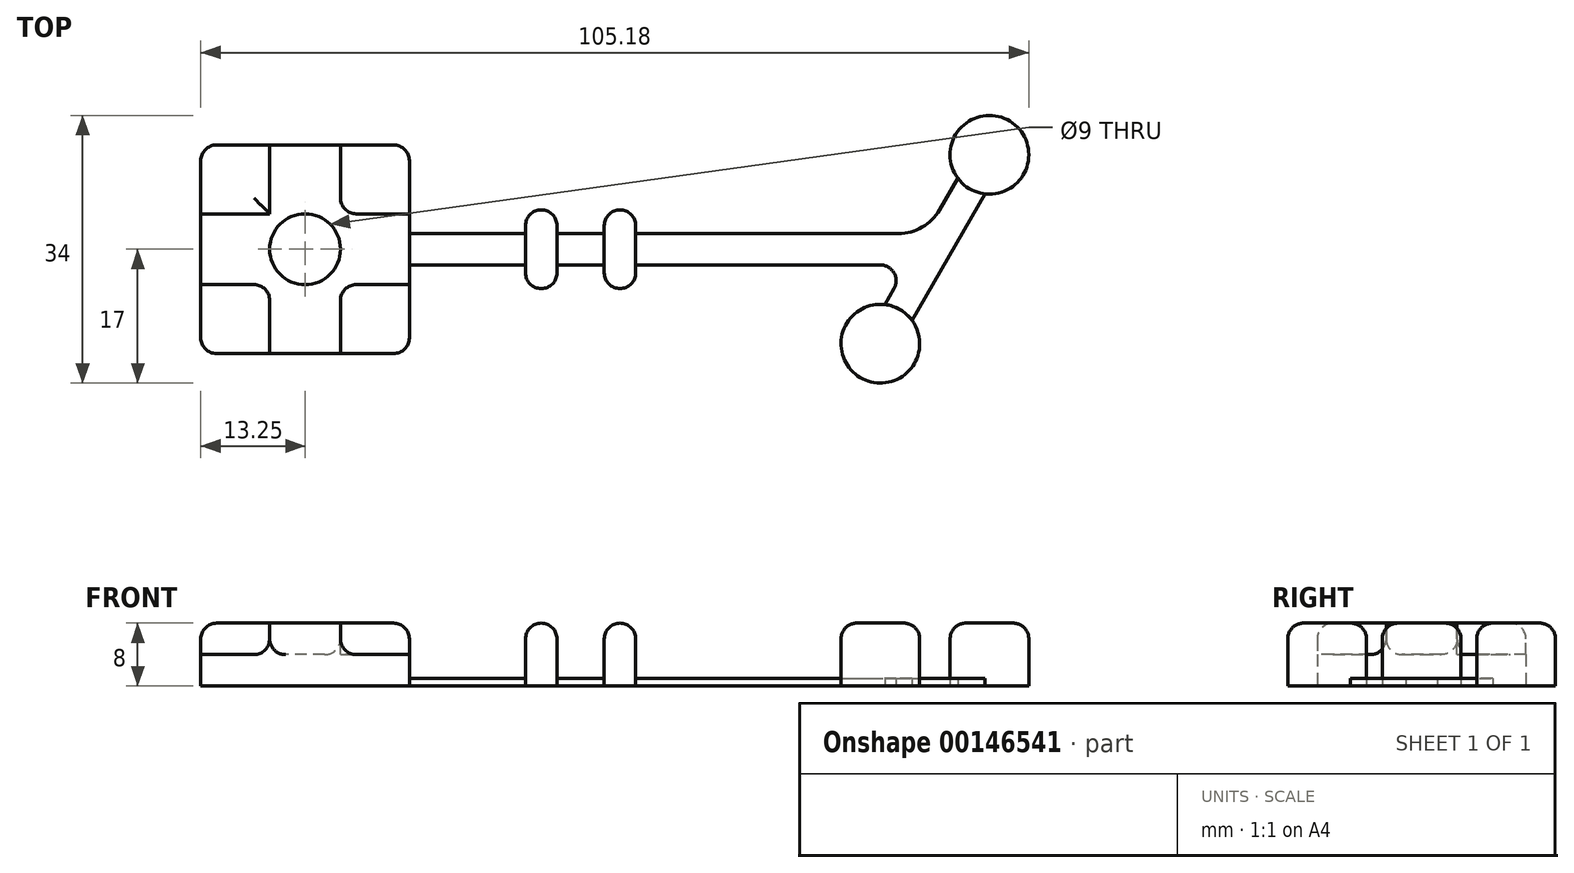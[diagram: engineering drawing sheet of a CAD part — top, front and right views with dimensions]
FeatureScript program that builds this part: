
annotation { "Feature Type Name" : "Feature", "Feature Type Description" : "" }
export const myFeature = defineFeature(function(context is Context, id is Id, definition is map)
    precondition{}
    {
        {
            var Q0;
            Q0=qCreatedBy(makeId("Top.planeOp"),FACE);
            var sketch = newSketch(context, id + "F0", { "sketchPlane" : qUnion([Q0])});
            skLineSegment(sketch, "E0.bottom", {"start": v(13.25, -13.25) * mm, "end": v(-13.25, -13.25) * mm});
            skLineSegment(sketch, "E0.top", {"start": v(13.25, 13.25) * mm, "end": v(-13.25, 13.25) * mm});
            skLineSegment(sketch, "E0.left", {"start": v(13.25, -13.25) * mm, "end": v(13.25, 13.25) * mm});
            skLineSegment(sketch, "E0.right", {"start": v(-13.25, -13.25) * mm, "end": v(-13.25, 13.25) * mm});
            skPoint(sketch, "E0.middle", {"position": v(0, 0) * mm});
            skLineSegment(sketch, "E1", {"start": v(0, 0) * mm, "end": v(80, 0) * mm, "construction": true});
            skLineSegment(sketch, "E2", {"start": v(80, 0) * mm, "end": v(86.93, 12) * mm, "construction": true});
            skCircle(sketch, "E3", {"center": v(86.93, 12) * mm, "radius": 5 * mm});
            skCircle(sketch, "E4", {"center": v(73.07, -12) * mm, "radius": 5 * mm});
            skLineSegment(sketch, "E5.bottom", {"start": v(32, -3) * mm, "end": v(28, -3) * mm});
            skLineSegment(sketch, "E5.top", {"start": v(32, 3) * mm, "end": v(28, 3) * mm});
            skLineSegment(sketch, "E5.left", {"start": v(32, -3) * mm, "end": v(32, 3) * mm});
            skLineSegment(sketch, "E5.right", {"start": v(28, -3) * mm, "end": v(28, 3) * mm});
            skPoint(sketch, "E5.middle", {"position": v(30, 0) * mm});
            skLineSegment(sketch, "E6.bottom", {"start": v(42, -3) * mm, "end": v(38, -3) * mm});
            skLineSegment(sketch, "E6.top", {"start": v(42, 3) * mm, "end": v(38, 3) * mm});
            skLineSegment(sketch, "E6.left", {"start": v(42, -3) * mm, "end": v(42, 3) * mm});
            skLineSegment(sketch, "E6.right", {"start": v(38, -3) * mm, "end": v(38, 3) * mm});
            skPoint(sketch, "E6.middle", {"position": v(40, 0) * mm});
            skLineSegment(sketch, "E7", {"start": v(13.25, 2) * mm, "end": v(28, 2) * mm});
            skLineSegment(sketch, "E8", {"start": v(32, 2) * mm, "end": v(38, 2) * mm});
            skLineSegment(sketch, "E9", {"start": v(42, 2) * mm, "end": v(78.85, 2) * mm});
            skLineSegment(sketch, "E10.MirrorCS", {"start": v(42, -2) * mm, "end": v(76.54, -2) * mm});
            skLineSegment(sketch, "E11.MirrorCS", {"start": v(32, -2) * mm, "end": v(38, -2) * mm});
            skLineSegment(sketch, "E12.MirrorCS", {"start": v(13.25, -2) * mm, "end": v(28, -2) * mm});
            skLineSegment(sketch, "E13.0", {"start": v(73.63, -7.03) * mm, "end": v(76.54, -2) * mm});
            skLineSegment(sketch, "E14.MirrorCS", {"start": v(77.1, -9.03) * mm, "end": v(86.37, 7.03) * mm});
            skLineSegment(sketch, "E15.trimOffspring", {"start": v(78.85, 2) * mm, "end": v(82.9, 9.03) * mm});
            skArc(sketch, "E16", {"start": v(32, 3) * mm, "mid": v(30, 5) * mm, "end": v(28, 3) * mm});
            skArc(sketch, "E17", {"start": v(38, 3) * mm, "mid": v(40, 5) * mm, "end": v(42, 3) * mm});
            skArc(sketch, "E18.MirrorCS", {"start": v(38, -3) * mm, "mid": v(40, -5) * mm, "end": v(42, -3) * mm});
            skArc(sketch, "E19.MirrorCS", {"start": v(32, -3) * mm, "mid": v(30, -5) * mm, "end": v(28, -3) * mm});
            skSolve(sketch);
        }
        {
            var Q0;
            {var subQ3=sQuery(id+"F0.wireOp",EDGE,"E0.bottom");Q0=makeQuery(id+"F0.imprint","IMPRINT",FACE,{"disambiguationData":[TD([[makeQuery(id+"F0.imprint","IMPRINT",EDGE,{"derivedFrom":subQ3}),-1.0]])]});}
            var Q1;
            Q1=makeQuery(id+"F0.imprint","IMPRINT",FACE,{"disambiguationData":[TD([[makeQuery(id+"F0.imprint","IMPRINT",EDGE,{"derivedFrom":sQuery(id+"F0.wireOp",EDGE,"E5.top")}),-1.0]])]});
            var Q2;
            {var subQ8=sQuery(id+"F0.wireOp",EDGE,"E5.bottom");Q2=makeQuery(id+"F0.imprint","IMPRINT",FACE,{"disambiguationData":[TD([[makeQuery(id+"F0.imprint","IMPRINT",EDGE,{"derivedFrom":subQ8}),-1.0]])]});}
            var Q3;
            Q3=makeQuery(id+"F0.imprint","IMPRINT",FACE,{"disambiguationData":[TD([[makeQuery(id+"F0.imprint","IMPRINT",EDGE,{"derivedFrom":sQuery(id+"F0.wireOp",EDGE,"E5.bottom")}),1.0]])]});
            var Q4;
            Q4=makeQuery(id+"F0.imprint","IMPRINT",FACE,{"disambiguationData":[TD([[makeQuery(id+"F0.imprint","IMPRINT",EDGE,{"derivedFrom":sQuery(id+"F0.wireOp",EDGE,"E6.top")}),-1.0]])]});
            var Q5;
            {var subQ4=sQuery(id+"F0.wireOp",EDGE,"E6.bottom");Q5=makeQuery(id+"F0.imprint","IMPRINT",FACE,{"disambiguationData":[TD([[makeQuery(id+"F0.imprint","IMPRINT",EDGE,{"derivedFrom":subQ4}),-1.0]])]});}
            var Q6;
            Q6=makeQuery(id+"F0.imprint","IMPRINT",FACE,{"disambiguationData":[TD([[makeQuery(id+"F0.imprint","IMPRINT",EDGE,{"derivedFrom":sQuery(id+"F0.wireOp",EDGE,"E6.bottom")}),1.0]])]});
            var Q7;
            {var subQ0=sQuery(id+"F0.wireOp",EDGE,"E3");var subQ1=makeQuery(id+"F0.imprint","INTERSECT",VERTEX,{"derivedFrom":[subQ0,sQuery(id+"F0.wireOp",EDGE,"E14.MirrorCS")]});Q7=makeQuery(id+"F0.imprint","IMPRINT",FACE,{"disambiguationData":[TD([[makeQuery(id+"F0.imprint","IMPRINT",EDGE,{"disambiguationData":[TD([[subQ1,1.0]])],"derivedFrom":subQ0}),1.0]])]});}
            var Q8;
            {var subQ0=sQuery(id+"F0.wireOp",EDGE,"E4");var subQ1=makeQuery(id+"F0.imprint","INTERSECT",VERTEX,{"derivedFrom":[subQ0,sQuery(id+"F0.wireOp",EDGE,"E13.0")]});Q8=makeQuery(id+"F0.imprint","IMPRINT",FACE,{"disambiguationData":[TD([[makeQuery(id+"F0.imprint","IMPRINT",EDGE,{"disambiguationData":[TD([[subQ1,1.0]])],"derivedFrom":subQ0}),1.0]])]});}
            extrude(context, id + "F1", {"entities" : qUnion([Q0, Q1, Q2, Q3, Q4, Q5, Q6, Q7, Q8]), "depth" : 8 * mm});
        }
        {
            var Q0;
            {var subQ0=sQuery(id+"F0.wireOp",EDGE,"E7");Q0=makeQuery(id+"F0.imprint","IMPRINT",FACE,{"disambiguationData":[TD([[makeQuery(id+"F0.imprint","IMPRINT",EDGE,{"derivedFrom":subQ0}),-1.0]])]});}
            var Q1;
            {var subQ0=sQuery(id+"F0.wireOp",EDGE,"E8");Q1=makeQuery(id+"F0.imprint","IMPRINT",FACE,{"disambiguationData":[TD([[makeQuery(id+"F0.imprint","IMPRINT",EDGE,{"derivedFrom":subQ0}),-1.0]])]});}
            var Q2;
            {var subQ0=sQuery(id+"F0.wireOp",EDGE,"E9");Q2=makeQuery(id+"F0.imprint","IMPRINT",FACE,{"disambiguationData":[TD([[makeQuery(id+"F0.imprint","IMPRINT",EDGE,{"derivedFrom":subQ0}),-1.0]])]});}
            extrude(context, id + "F2", {"entities" : qUnion([Q0, Q1, Q2]), "operationType" : NewBodyOperationType.ADD, "depth" : 1 * mm});
        }
        {
            var Q0;
            Q0=makeQuery(id+"F1.opExtrude","CAP_FACE",FACE,{"disambiguationData":[OSD([sQuery(id+"F0.wireOp",EDGE,"E5.left"),sQuery(id+"F0.wireOp",EDGE,"E5.right"),sQuery(id+"F0.wireOp",EDGE,"E16"),sQuery(id+"F0.wireOp",EDGE,"E19.MirrorCS")])],"isStart":false});
            var Q1;
            Q1=makeQuery(id+"F1.opExtrude","CAP_FACE",FACE,{"disambiguationData":[OSD([sQuery(id+"F0.wireOp",EDGE,"E6.left"),sQuery(id+"F0.wireOp",EDGE,"E6.right"),sQuery(id+"F0.wireOp",EDGE,"E17"),sQuery(id+"F0.wireOp",EDGE,"E18.MirrorCS")])],"isStart":false});
            var Q2;
            Q2=makeQuery(id+"F1.opExtrude","CAP_FACE",FACE,{"disambiguationData":[OSD([sQuery(id+"F0.wireOp",EDGE,"E3")])],"isStart":false});
            var Q3;
            Q3=makeQuery(id+"F1.opExtrude","CAP_FACE",FACE,{"disambiguationData":[OSD([sQuery(id+"F0.wireOp",EDGE,"E4")])],"isStart":false});
            fillet(context, id + "F3", {"entities" : qUnion([Q0, Q1, Q2, Q3]), "radius" : 2 * mm, "tangentPropagation" : true, "allowEdgeOverflow" : false});
        }
        {
            var Q0;
            Q0=makeQuery(id+"F2.opExtrude","SWEPT_EDGE",EDGE,{"disambiguationData":[OSD([sQuery(id+"F0.wireOp",EDGE,"E0.left"),sQuery(id+"F0.wireOp",EDGE,"E12.MirrorCS")])]});
            var Q1;
            Q1=makeQuery(id+"F2.opExtrude","SWEPT_EDGE",EDGE,{"disambiguationData":[OSD([sQuery(id+"F0.wireOp",EDGE,"E5.right"),sQuery(id+"F0.wireOp",EDGE,"E12.MirrorCS")])]});
            var Q2;
            Q2=makeQuery(id+"F2.opExtrude","SWEPT_EDGE",EDGE,{"disambiguationData":[OSD([sQuery(id+"F0.wireOp",EDGE,"E6.right"),sQuery(id+"F0.wireOp",EDGE,"E11.MirrorCS")])]});
            var Q3;
            Q3=makeQuery(id+"F2.opExtrude","SWEPT_EDGE",EDGE,{"disambiguationData":[OSD([sQuery(id+"F0.wireOp",EDGE,"E5.left"),sQuery(id+"F0.wireOp",EDGE,"E11.MirrorCS")])]});
            var Q4;
            Q4=makeQuery(id+"F2.opExtrude","SWEPT_EDGE",EDGE,{"disambiguationData":[OSD([sQuery(id+"F0.wireOp",EDGE,"E6.left"),sQuery(id+"F0.wireOp",EDGE,"E10.MirrorCS")])]});
            var Q5;
            Q5=makeQuery(id+"F2.opExtrude","SWEPT_EDGE",EDGE,{"disambiguationData":[OSD([sQuery(id+"F0.wireOp",EDGE,"E0.left"),sQuery(id+"F0.wireOp",EDGE,"E7")])]});
            var Q6;
            Q6=makeQuery(id+"F2.opExtrude","SWEPT_EDGE",EDGE,{"disambiguationData":[OSD([sQuery(id+"F0.wireOp",EDGE,"E5.left"),sQuery(id+"F0.wireOp",EDGE,"E8")])]});
            var Q7;
            Q7=makeQuery(id+"F2.opExtrude","SWEPT_EDGE",EDGE,{"disambiguationData":[OSD([sQuery(id+"F0.wireOp",EDGE,"E6.left"),sQuery(id+"F0.wireOp",EDGE,"E9")])]});
            var Q8;
            Q8=makeQuery(id+"F2.opExtrude","SWEPT_EDGE",EDGE,{"disambiguationData":[OSD([sQuery(id+"F0.wireOp",EDGE,"E4"),sQuery(id+"F0.wireOp",EDGE,"E14.MirrorCS")])]});
            var Q9;
            Q9=makeQuery(id+"F2.opExtrude","SWEPT_EDGE",EDGE,{"disambiguationData":[OSD([sQuery(id+"F0.wireOp",EDGE,"E3"),sQuery(id+"F0.wireOp",EDGE,"E14.MirrorCS")])]});
            var Q10;
            Q10=makeQuery(id+"F2.opExtrude","SWEPT_EDGE",EDGE,{"disambiguationData":[OSD([sQuery(id+"F0.wireOp",EDGE,"E10.MirrorCS"),sQuery(id+"F0.wireOp",EDGE,"E13.0")])]});
            var Q11;
            Q11=makeQuery(id+"F2.opExtrude","SWEPT_EDGE",EDGE,{"disambiguationData":[OSD([sQuery(id+"F0.wireOp",EDGE,"E5.right"),sQuery(id+"F0.wireOp",EDGE,"E7")])]});
            var Q12;
            Q12=makeQuery(id+"F2.opExtrude","SWEPT_EDGE",EDGE,{"disambiguationData":[OSD([sQuery(id+"F0.wireOp",EDGE,"E6.right"),sQuery(id+"F0.wireOp",EDGE,"E8")])]});
            fillet(context, id + "F4", {"entities" : qUnion([Q0, Q1, Q2, Q3, Q4, Q5, Q6, Q7, Q8, Q9, Q10, Q11, Q12]), "radius" : 2 * mm, "tangentPropagation" : true, "allowEdgeOverflow" : false});
        }
        {
            var Q0;
            Q0=makeQuery(id+"F2.opExtrude","SWEPT_EDGE",EDGE,{"disambiguationData":[OSD([sQuery(id+"F0.wireOp",EDGE,"E9"),sQuery(id+"F0.wireOp",EDGE,"E15.trimOffspring")])]});
            fillet(context, id + "F5", {"entities" : qUnion([Q0]), "radius" : 6 * mm, "tangentPropagation" : true, "allowEdgeOverflow" : false});
        }
        {
            var Q0;
            Q0=makeQuery(id+"F1.opExtrude","CAP_FACE",FACE,{"disambiguationData":[OSD([sQuery(id+"F0.wireOp",EDGE,"E0.bottom"),sQuery(id+"F0.wireOp",EDGE,"E0.top"),sQuery(id+"F0.wireOp",EDGE,"E0.left"),sQuery(id+"F0.wireOp",EDGE,"E0.right")])],"isStart":false});
            var sketch = newSketch(context, id + "F6", { "sketchPlane" : qUnion([Q0])});
            skCircle(sketch, "E20", {"center": v(0, 0) * mm, "radius": 4.5 * mm});
            skLineSegment(sketch, "E21", {"start": v(13.25, 4.5) * mm, "end": v(4.5, 4.5) * mm});
            skLineSegment(sketch, "E22", {"start": v(13.25, -4.5) * mm, "end": v(4.5, -4.5) * mm});
            skLineSegment(sketch, "E23", {"start": v(4.5, 13.25) * mm, "end": v(4.5, 4.5) * mm});
            skLineSegment(sketch, "E24", {"start": v(-4.5, 13.25) * mm, "end": v(-4.5, 4.5) * mm});
            skLineSegment(sketch, "E25.trimOffspring", {"start": v(-4.5, -4.5) * mm, "end": v(-4.5, -13.25) * mm});
            skLineSegment(sketch, "E26.trimOffspring", {"start": v(-4.5, 4.5) * mm, "end": v(-13.25, 4.5) * mm});
            skLineSegment(sketch, "E27.trimOffspring", {"start": v(-4.5, -4.5) * mm, "end": v(-13.25, -4.5) * mm});
            skLineSegment(sketch, "E28.trimOffspring", {"start": v(4.5, -4.5) * mm, "end": v(4.5, -13.25) * mm});
            skSolve(sketch);
        }
        {
            var Q0;
            {var subQ0=sQuery(id+"F6.wireOp",EDGE,"E24");Q0=makeQuery(id+"F6.imprint","IMPRINT",FACE,{"disambiguationData":[TD([[makeQuery(id+"F6.imprint","IMPRINT",EDGE,{"derivedFrom":subQ0}),-1.0]])]});}
            var Q1;
            {var subQ0=sQuery(id+"F6.wireOp",EDGE,"E21");Q1=makeQuery(id+"F6.imprint","IMPRINT",FACE,{"disambiguationData":[TD([[makeQuery(id+"F6.imprint","IMPRINT",EDGE,{"derivedFrom":subQ0}),-1.0]])]});}
            var Q2;
            {var subQ0=sQuery(id+"F6.wireOp",EDGE,"E22");Q2=makeQuery(id+"F6.imprint","IMPRINT",FACE,{"disambiguationData":[TD([[makeQuery(id+"F6.imprint","IMPRINT",EDGE,{"derivedFrom":subQ0}),1.0]])]});}
            var Q3;
            {var subQ0=sQuery(id+"F6.wireOp",EDGE,"E25.trimOffspring");Q3=makeQuery(id+"F6.imprint","IMPRINT",FACE,{"disambiguationData":[TD([[makeQuery(id+"F6.imprint","IMPRINT",EDGE,{"derivedFrom":subQ0}),-1.0]])]});}
            var Q4;
            Q4=makeQuery(id+"F6.imprint","IMPRINT",FACE,{"disambiguationData":[TD([[makeQuery(id+"F6.imprint","IMPRINT",EDGE,{"derivedFrom":sQuery(id+"F6.wireOp",EDGE,"E20")}),1.0]])]});
            extrude(context, id + "F7", {"entities" : qUnion([Q0, Q1, Q2, Q3, Q4]), "operationType" : NewBodyOperationType.REMOVE, "oppositeDirection" : true, "depth" : 4 * mm});
        }
        {
            var Q0;
            Q0=makeQuery(id+"F7.boolean.opBoolean","COPY",EDGE,{"derivedFrom":makeQuery(id+"F7.opExtrude","CAP_EDGE",EDGE,{"disambiguationData":[OSD([sQuery(id+"F6.wireOp",EDGE,"E24")])],"isStart":false})});
            var Q1;
            Q1=makeQuery(id+"F7.boolean.opBoolean","COPY",EDGE,{"derivedFrom":makeQuery(id+"F7.opExtrude","CAP_EDGE",EDGE,{"disambiguationData":[OSD([sQuery(id+"F6.wireOp",EDGE,"E26.trimOffspring")])],"isStart":false})});
            var Q2;
            Q2=makeQuery(id+"F7.boolean.opBoolean","COPY",EDGE,{"derivedFrom":makeQuery(id+"F7.opExtrude","CAP_EDGE",EDGE,{"disambiguationData":[OSD([sQuery(id+"F6.wireOp",EDGE,"E27.trimOffspring")])],"isStart":false})});
            var Q3;
            Q3=makeQuery(id+"F7.boolean.opBoolean","COPY",EDGE,{"derivedFrom":makeQuery(id+"F7.opExtrude","CAP_EDGE",EDGE,{"disambiguationData":[OSD([sQuery(id+"F6.wireOp",EDGE,"E25.trimOffspring")])],"isStart":false})});
            var Q4;
            Q4=makeQuery(id+"F7.boolean.opBoolean","COPY",EDGE,{"derivedFrom":makeQuery(id+"F7.opExtrude","CAP_EDGE",EDGE,{"disambiguationData":[OSD([sQuery(id+"F6.wireOp",EDGE,"E25.trimOffspring")])],"isStart":true})});
            var Q5;
            Q5=makeQuery(id+"F7.boolean.opBoolean","COPY",EDGE,{"derivedFrom":makeQuery(id+"F7.opExtrude","CAP_EDGE",EDGE,{"disambiguationData":[OSD([sQuery(id+"F6.wireOp",EDGE,"E27.trimOffspring")])],"isStart":true})});
            var Q6;
            Q6=makeQuery(id+"F7.boolean.opBoolean","COPY",EDGE,{"derivedFrom":makeQuery(id+"F7.opExtrude","CAP_EDGE",EDGE,{"disambiguationData":[OSD([sQuery(id+"F6.wireOp",EDGE,"E26.trimOffspring")])],"isStart":true})});
            var Q7;
            Q7=makeQuery(id+"F7.boolean.opBoolean","COPY",EDGE,{"derivedFrom":makeQuery(id+"F7.opExtrude","CAP_EDGE",EDGE,{"disambiguationData":[OSD([sQuery(id+"F6.wireOp",EDGE,"E24")])],"isStart":true})});
            var Q8;
            Q8=makeQuery(id+"F7.boolean.opBoolean","COPY",EDGE,{"derivedFrom":makeQuery(id+"F7.opExtrude","CAP_EDGE",EDGE,{"disambiguationData":[OSD([sQuery(id+"F6.wireOp",EDGE,"E23")])],"isStart":true})});
            var Q9;
            Q9=makeQuery(id+"F7.boolean.opBoolean","COPY",EDGE,{"derivedFrom":makeQuery(id+"F7.opExtrude","CAP_EDGE",EDGE,{"disambiguationData":[OSD([sQuery(id+"F6.wireOp",EDGE,"E21")])],"isStart":true})});
            var Q10;
            Q10=makeQuery(id+"F7.boolean.opBoolean","COPY",EDGE,{"derivedFrom":makeQuery(id+"F7.opExtrude","CAP_EDGE",EDGE,{"disambiguationData":[OSD([sQuery(id+"F6.wireOp",EDGE,"E22")])],"isStart":true})});
            var Q11;
            Q11=makeQuery(id+"F7.boolean.opBoolean","COPY",EDGE,{"derivedFrom":makeQuery(id+"F7.opExtrude","CAP_EDGE",EDGE,{"disambiguationData":[OSD([sQuery(id+"F6.wireOp",EDGE,"E28.trimOffspring")])],"isStart":true})});
            var Q12;
            Q12=makeQuery(id+"F1.opExtrude","CAP_EDGE",EDGE,{"disambiguationData":[OSD([sQuery(id+"F0.wireOp",EDGE,"E0.bottom")])],"isStart":false});
            var Q13;
            Q13=makeQuery(id+"F1.opExtrude","CAP_EDGE",EDGE,{"disambiguationData":[OSD([sQuery(id+"F0.wireOp",EDGE,"E0.top")])],"isStart":false});
            var Q14;
            {var subQ0=sQuery(id+"F0.wireOp",EDGE,"E0.top");var subQ1=makeQuery(id+"F1.opExtrude","CAP_EDGE",EDGE,{"disambiguationData":[OSD([subQ0])],"isStart":false});Q14=makeQuery(id+"F7.boolean.opBoolean","COPY",EDGE,{"derivedFrom":makeQuery(id+"F7.opExtrude","CAP_EDGE",EDGE,{"disambiguationData":[OSD([subQ0]),TDD([makeQuery(id+"F6.imprint","IMPRINT",EDGE,{"disambiguationData":[TD([[makeQuery(id+"F6.imprint","INTERSECT",VERTEX,{"derivedFrom":[subQ1,makeQuery(id+"F1.opExtrude","CAP_EDGE",EDGE,{"disambiguationData":[OSD([sQuery(id+"F0.wireOp",EDGE,"E0.right")])],"isStart":false})]}),1.0]])],"derivedFrom":subQ1})])],"isStart":false})});}
            var Q15;
            {var subQ0=sQuery(id+"F0.wireOp",EDGE,"E0.right");var subQ1=makeQuery(id+"F1.opExtrude","CAP_EDGE",EDGE,{"disambiguationData":[OSD([subQ0])],"isStart":false});Q15=makeQuery(id+"F7.boolean.opBoolean","COPY",EDGE,{"derivedFrom":makeQuery(id+"F7.opExtrude","CAP_EDGE",EDGE,{"disambiguationData":[OSD([subQ0]),TDD([makeQuery(id+"F6.imprint","IMPRINT",EDGE,{"disambiguationData":[TD([[makeQuery(id+"F6.imprint","INTERSECT",VERTEX,{"derivedFrom":[makeQuery(id+"F1.opExtrude","CAP_EDGE",EDGE,{"disambiguationData":[OSD([sQuery(id+"F0.wireOp",EDGE,"E0.top")])],"isStart":false}),subQ1]}),1.0]])],"derivedFrom":subQ1})])],"isStart":false})});}
            var Q16;
            {var subQ0=sQuery(id+"F0.wireOp",EDGE,"E0.right");var subQ1=makeQuery(id+"F1.opExtrude","CAP_EDGE",EDGE,{"disambiguationData":[OSD([subQ0])],"isStart":false});Q16=makeQuery(id+"F7.boolean.opBoolean","COPY",EDGE,{"derivedFrom":makeQuery(id+"F7.opExtrude","CAP_EDGE",EDGE,{"disambiguationData":[OSD([subQ0]),TDD([makeQuery(id+"F6.imprint","IMPRINT",EDGE,{"disambiguationData":[TD([[makeQuery(id+"F6.imprint","INTERSECT",VERTEX,{"derivedFrom":[makeQuery(id+"F1.opExtrude","CAP_EDGE",EDGE,{"disambiguationData":[OSD([sQuery(id+"F0.wireOp",EDGE,"E0.bottom")])],"isStart":false}),subQ1]}),-1.0]])],"derivedFrom":subQ1})])],"isStart":false})});}
            var Q17;
            {var subQ0=sQuery(id+"F0.wireOp",EDGE,"E0.bottom");var subQ1=makeQuery(id+"F1.opExtrude","CAP_EDGE",EDGE,{"disambiguationData":[OSD([subQ0])],"isStart":false});Q17=makeQuery(id+"F7.boolean.opBoolean","COPY",EDGE,{"derivedFrom":makeQuery(id+"F7.opExtrude","CAP_EDGE",EDGE,{"disambiguationData":[OSD([subQ0]),TDD([makeQuery(id+"F6.imprint","IMPRINT",EDGE,{"disambiguationData":[TD([[makeQuery(id+"F6.imprint","INTERSECT",VERTEX,{"derivedFrom":[subQ1,makeQuery(id+"F1.opExtrude","CAP_EDGE",EDGE,{"disambiguationData":[OSD([sQuery(id+"F0.wireOp",EDGE,"E0.right")])],"isStart":false})]}),1.0]])],"derivedFrom":subQ1})])],"isStart":false})});}
            var Q18;
            {var subQ0=sQuery(id+"F0.wireOp",EDGE,"E0.bottom");var subQ1=makeQuery(id+"F1.opExtrude","CAP_EDGE",EDGE,{"disambiguationData":[OSD([subQ0])],"isStart":false});Q18=makeQuery(id+"F7.boolean.opBoolean","COPY",EDGE,{"derivedFrom":makeQuery(id+"F7.opExtrude","CAP_EDGE",EDGE,{"disambiguationData":[OSD([subQ0]),TDD([makeQuery(id+"F6.imprint","IMPRINT",EDGE,{"disambiguationData":[TD([[makeQuery(id+"F6.imprint","INTERSECT",VERTEX,{"derivedFrom":[subQ1,makeQuery(id+"F1.opExtrude","CAP_EDGE",EDGE,{"disambiguationData":[OSD([sQuery(id+"F0.wireOp",EDGE,"E0.left")])],"isStart":false})]}),-1.0]])],"derivedFrom":subQ1})])],"isStart":false})});}
            var Q19;
            {var subQ0=sQuery(id+"F0.wireOp",EDGE,"E0.left");var subQ1=makeQuery(id+"F1.opExtrude","CAP_EDGE",EDGE,{"disambiguationData":[OSD([subQ0])],"isStart":false});Q19=makeQuery(id+"F7.boolean.opBoolean","COPY",EDGE,{"derivedFrom":makeQuery(id+"F7.opExtrude","CAP_EDGE",EDGE,{"disambiguationData":[OSD([subQ0]),TDD([makeQuery(id+"F6.imprint","IMPRINT",EDGE,{"disambiguationData":[TD([[makeQuery(id+"F6.imprint","INTERSECT",VERTEX,{"derivedFrom":[makeQuery(id+"F1.opExtrude","CAP_EDGE",EDGE,{"disambiguationData":[OSD([sQuery(id+"F0.wireOp",EDGE,"E0.bottom")])],"isStart":false}),subQ1]}),-1.0]])],"derivedFrom":subQ1})])],"isStart":false})});}
            var Q20;
            {var subQ0=sQuery(id+"F0.wireOp",EDGE,"E0.left");var subQ1=makeQuery(id+"F1.opExtrude","CAP_EDGE",EDGE,{"disambiguationData":[OSD([subQ0])],"isStart":false});Q20=makeQuery(id+"F7.boolean.opBoolean","COPY",EDGE,{"derivedFrom":makeQuery(id+"F7.opExtrude","CAP_EDGE",EDGE,{"disambiguationData":[OSD([subQ0]),TDD([makeQuery(id+"F6.imprint","IMPRINT",EDGE,{"disambiguationData":[TD([[makeQuery(id+"F6.imprint","INTERSECT",VERTEX,{"derivedFrom":[makeQuery(id+"F1.opExtrude","CAP_EDGE",EDGE,{"disambiguationData":[OSD([sQuery(id+"F0.wireOp",EDGE,"E0.top")])],"isStart":false}),subQ1]}),1.0]])],"derivedFrom":subQ1})])],"isStart":false})});}
            var Q21;
            {var subQ0=sQuery(id+"F0.wireOp",EDGE,"E0.top");var subQ1=makeQuery(id+"F1.opExtrude","CAP_EDGE",EDGE,{"disambiguationData":[OSD([subQ0])],"isStart":false});Q21=makeQuery(id+"F7.boolean.opBoolean","COPY",EDGE,{"derivedFrom":makeQuery(id+"F7.opExtrude","CAP_EDGE",EDGE,{"disambiguationData":[OSD([subQ0]),TDD([makeQuery(id+"F6.imprint","IMPRINT",EDGE,{"disambiguationData":[TD([[makeQuery(id+"F6.imprint","INTERSECT",VERTEX,{"derivedFrom":[subQ1,makeQuery(id+"F1.opExtrude","CAP_EDGE",EDGE,{"disambiguationData":[OSD([sQuery(id+"F0.wireOp",EDGE,"E0.left")])],"isStart":false})]}),-1.0]])],"derivedFrom":subQ1})])],"isStart":false})});}
            var Q22;
            Q22=makeQuery(id+"F1.opExtrude","CAP_EDGE",EDGE,{"disambiguationData":[OSD([sQuery(id+"F0.wireOp",EDGE,"E0.left")])],"isStart":false});
            var Q23;
            Q23=makeQuery(id+"F1.opExtrude","CAP_EDGE",EDGE,{"disambiguationData":[OSD([sQuery(id+"F0.wireOp",EDGE,"E0.right")])],"isStart":false});
            var Q24;
            Q24=makeQuery(id+"F7.boolean.opBoolean","COPY",EDGE,{"derivedFrom":makeQuery(id+"F7.opExtrude","SWEPT_EDGE",EDGE,{"disambiguationData":[OSD([sQuery(id+"F0.wireOp",EDGE,"E0.left"),sQuery(id+"F6.wireOp",EDGE,"E22")])]})});
            var Q25;
            Q25=makeQuery(id+"F7.boolean.opBoolean","COPY",EDGE,{"derivedFrom":makeQuery(id+"F7.opExtrude","SWEPT_EDGE",EDGE,{"disambiguationData":[OSD([sQuery(id+"F0.wireOp",EDGE,"E0.left"),sQuery(id+"F6.wireOp",EDGE,"E21")])]})});
            var Q26;
            Q26=makeQuery(id+"F7.boolean.opBoolean","COPY",EDGE,{"derivedFrom":makeQuery(id+"F7.opExtrude","SWEPT_EDGE",EDGE,{"disambiguationData":[OSD([sQuery(id+"F0.wireOp",EDGE,"E0.top"),sQuery(id+"F6.wireOp",EDGE,"E23")])]})});
            var Q27;
            Q27=makeQuery(id+"F7.boolean.opBoolean","COPY",EDGE,{"derivedFrom":makeQuery(id+"F7.opExtrude","SWEPT_EDGE",EDGE,{"disambiguationData":[OSD([sQuery(id+"F0.wireOp",EDGE,"E0.bottom"),sQuery(id+"F6.wireOp",EDGE,"E28.trimOffspring")])]})});
            var Q28;
            Q28=makeQuery(id+"F1.opExtrude","SWEPT_EDGE",EDGE,{"disambiguationData":[OSD([sQuery(id+"F0.wireOp",EDGE,"E0.bottom"),sQuery(id+"F0.wireOp",EDGE,"E0.right")])]});
            var Q29;
            Q29=makeQuery(id+"F1.opExtrude","SWEPT_EDGE",EDGE,{"disambiguationData":[OSD([sQuery(id+"F0.wireOp",EDGE,"E0.bottom"),sQuery(id+"F0.wireOp",EDGE,"E0.left")])]});
            var Q30;
            Q30=makeQuery(id+"F1.opExtrude","SWEPT_EDGE",EDGE,{"disambiguationData":[OSD([sQuery(id+"F0.wireOp",EDGE,"E0.top"),sQuery(id+"F0.wireOp",EDGE,"E0.right")])]});
            var Q31;
            Q31=makeQuery(id+"F1.opExtrude","SWEPT_EDGE",EDGE,{"disambiguationData":[OSD([sQuery(id+"F0.wireOp",EDGE,"E0.top"),sQuery(id+"F0.wireOp",EDGE,"E0.left")])]});
            var Q32;
            Q32=makeQuery(id+"F7.boolean.opBoolean","COPY",EDGE,{"derivedFrom":makeQuery(id+"F7.opExtrude","CAP_EDGE",EDGE,{"disambiguationData":[OSD([sQuery(id+"F6.wireOp",EDGE,"E20")])],"isStart":false})});
            var Q33;
            Q33=makeQuery(id+"F7.boolean.opBoolean","COPY",EDGE,{"derivedFrom":makeQuery(id+"F7.opExtrude","CAP_EDGE",EDGE,{"disambiguationData":[OSD([sQuery(id+"F6.wireOp",EDGE,"E20")])],"isStart":true})});
            var Q34;
            Q34=makeQuery(id+"F7.boolean.opBoolean","COPY",EDGE,{"derivedFrom":makeQuery(id+"F7.opExtrude","SWEPT_EDGE",EDGE,{"disambiguationData":[OSD([sQuery(id+"F6.wireOp",EDGE,"E22"),sQuery(id+"F6.wireOp",EDGE,"E28.trimOffspring")])]})});
            var Q35;
            Q35=makeQuery(id+"F7.boolean.opBoolean","COPY",EDGE,{"derivedFrom":makeQuery(id+"F7.opExtrude","SWEPT_EDGE",EDGE,{"disambiguationData":[OSD([sQuery(id+"F6.wireOp",EDGE,"E21"),sQuery(id+"F6.wireOp",EDGE,"E23")])]})});
            var Q36;
            Q36=makeQuery(id+"F7.boolean.opBoolean","COPY",EDGE,{"derivedFrom":makeQuery(id+"F7.opExtrude","SWEPT_EDGE",EDGE,{"disambiguationData":[OSD([sQuery(id+"F0.wireOp",EDGE,"E0.right"),sQuery(id+"F6.wireOp",EDGE,"E26.trimOffspring")])]})});
            fillet(context, id + "F8", {"entities" : qUnion([Q0, Q1, Q2, Q3, Q4, Q5, Q6, Q7, Q8, Q9, Q10, Q11, Q12, Q13, Q14, Q15, Q16, Q17, Q18, Q19, Q20, Q21, Q22, Q23, Q24, Q25, Q26, Q27, Q28, Q29, Q30, Q31, Q32, Q33, Q34, Q35, Q36]), "radius" : 2 * mm, "tangentPropagation" : true, "allowEdgeOverflow" : false});
        }
        {
            var Q0;
            {var subQ0=sQuery(id+"F0.wireOp",EDGE,"E0.bottom");var subQ1=makeQuery(id+"F1.opExtrude","CAP_EDGE",EDGE,{"disambiguationData":[OSD([subQ0])],"isStart":false});var subQ2=sQuery(id+"F6.wireOp",EDGE,"E28.trimOffspring");Q0=makeQuery(id+"F8.opFillet","BLEND_EDGE",EDGE,{"blendedFrom":[makeQuery(id+"F7.boolean.opBoolean","COPY",EDGE,{"derivedFrom":makeQuery(id+"F7.opExtrude","SWEPT_EDGE",EDGE,{"disambiguationData":[OSD([subQ0,subQ2])]})}),makeQuery(id+"F7.boolean.opBoolean","COPY",EDGE,{"derivedFrom":makeQuery(id+"F7.opExtrude","CAP_EDGE",EDGE,{"disambiguationData":[OSD([subQ0]),TDD([makeQuery(id+"F6.imprint","IMPRINT",EDGE,{"disambiguationData":[TD([[makeQuery(id+"F6.imprint","INTERSECT",VERTEX,{"derivedFrom":[subQ1,makeQuery(id+"F1.opExtrude","CAP_EDGE",EDGE,{"disambiguationData":[OSD([sQuery(id+"F0.wireOp",EDGE,"E0.left")])],"isStart":false})]}),-1.0]])],"derivedFrom":subQ1})])],"isStart":false})})],"blendedInto":[]});}
            var Q1;
            Q1=makeQuery(id+"F7.boolean.opBoolean","COPY",EDGE,{"derivedFrom":makeQuery(id+"F7.opExtrude","CAP_EDGE",EDGE,{"disambiguationData":[OSD([sQuery(id+"F6.wireOp",EDGE,"E28.trimOffspring")])],"isStart":false})});
            var Q2;
            {var subQ0=sQuery(id+"F6.wireOp",EDGE,"E28.trimOffspring");var subQ1=sQuery(id+"F6.wireOp",EDGE,"E22");Q2=makeQuery(id+"F8.opFillet","BLEND_EDGE",EDGE,{"blendedFrom":[makeQuery(id+"F7.boolean.opBoolean","COPY",EDGE,{"derivedFrom":makeQuery(id+"F7.opExtrude","SWEPT_EDGE",EDGE,{"disambiguationData":[OSD([subQ1,subQ0])]})}),makeQuery(id+"F7.boolean.opBoolean","COPY",FACE,{"derivedFrom":makeQuery(id+"F7.opExtrude","CAP_FACE",FACE,{"disambiguationData":[OSD([sQuery(id+"F0.wireOp",EDGE,"E0.bottom"),sQuery(id+"F0.wireOp",EDGE,"E0.left"),subQ1,subQ0])],"isStart":false})})],"blendedInto":[makeQuery(id+"F7.boolean.opBoolean","COPY",FACE,{"derivedFrom":makeQuery(id+"F7.opExtrude","CAP_FACE",FACE,{"disambiguationData":[OSD([sQuery(id+"F0.wireOp",EDGE,"E0.bottom"),sQuery(id+"F0.wireOp",EDGE,"E0.left"),subQ1,subQ0])],"isStart":false})})]});}
            var Q3;
            Q3=makeQuery(id+"F7.boolean.opBoolean","COPY",EDGE,{"derivedFrom":makeQuery(id+"F7.opExtrude","CAP_EDGE",EDGE,{"disambiguationData":[OSD([sQuery(id+"F6.wireOp",EDGE,"E22")])],"isStart":false})});
            var Q4;
            {var subQ0=sQuery(id+"F0.wireOp",EDGE,"E0.left");var subQ1=makeQuery(id+"F1.opExtrude","CAP_EDGE",EDGE,{"disambiguationData":[OSD([subQ0])],"isStart":false});var subQ2=sQuery(id+"F6.wireOp",EDGE,"E22");Q4=makeQuery(id+"F8.opFillet","BLEND_EDGE",EDGE,{"blendedFrom":[makeQuery(id+"F7.boolean.opBoolean","COPY",EDGE,{"derivedFrom":makeQuery(id+"F7.opExtrude","SWEPT_EDGE",EDGE,{"disambiguationData":[OSD([subQ0,subQ2])]})}),makeQuery(id+"F7.boolean.opBoolean","COPY",EDGE,{"derivedFrom":makeQuery(id+"F7.opExtrude","CAP_EDGE",EDGE,{"disambiguationData":[OSD([subQ0]),TDD([makeQuery(id+"F6.imprint","IMPRINT",EDGE,{"disambiguationData":[TD([[makeQuery(id+"F6.imprint","INTERSECT",VERTEX,{"derivedFrom":[makeQuery(id+"F1.opExtrude","CAP_EDGE",EDGE,{"disambiguationData":[OSD([sQuery(id+"F0.wireOp",EDGE,"E0.bottom")])],"isStart":false}),subQ1]}),-1.0]])],"derivedFrom":subQ1})])],"isStart":false})})],"blendedInto":[]});}
            var Q5;
            Q5=makeQuery(id+"F8.opFillet","BLEND_EDGE",EDGE,{"blendedFrom":[makeQuery(id+"F7.boolean.opBoolean","COPY",EDGE,{"derivedFrom":makeQuery(id+"F7.opExtrude","CAP_EDGE",EDGE,{"disambiguationData":[OSD([sQuery(id+"F6.wireOp",EDGE,"E25.trimOffspring")])],"isStart":false})}),makeQuery(id+"F7.boolean.opBoolean","COPY",EDGE,{"derivedFrom":makeQuery(id+"F7.opExtrude","CAP_EDGE",EDGE,{"disambiguationData":[OSD([sQuery(id+"F6.wireOp",EDGE,"E27.trimOffspring")])],"isStart":false})})],"blendedInto":[]});
            fillet(context, id + "F9", {"entities" : qUnion([Q0, Q1, Q2, Q3, Q4, Q5]), "radius" : 2 * mm, "tangentPropagation" : true, "allowEdgeOverflow" : false});
        }
    });
